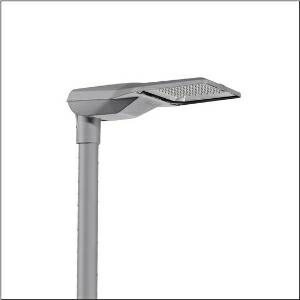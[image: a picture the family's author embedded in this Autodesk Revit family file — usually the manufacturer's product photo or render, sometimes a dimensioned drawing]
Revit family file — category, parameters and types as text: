
# Revit family: streetlight_sl_21_iq_midi___stw1_0a_5xe3e31g08nb_66c1
name_source: partatom
category: Lighting Fixtures
units: mm (PartAtom-declared; Revit-internal decimal feet)

## family parameters
Cut with Voids When Loaded = No
Host = Face
Light Source = No
Part Type = Normal
Room Calculation Point = No
Round Connector Dimension = Use Diameter
Shared = No

## types (1)
- --- (1 x LED, 23230 lm, 155.5 W, 3000K)
    Apparent Load = 155 VA
    CIE Flux Codes = 39 75 98 100 100
    Color Rendering = 70
    Color Temperature = 3000K
    Default Elevation = 1800 mm
    Description = Streetlight SL 21 iQ midi, mast luminaire, primary light control with lens, of PMMA, primary optical cover: cover, of toughened safety glass, transparent, light distribution: STW1.0a, light emission: direct distribution, primary light characteristic: asymmetric, installation type: post-top, side-entry, LED, High Power LED, rated luminous flux: 23.230lm, luminous efficacy: 149lm/W, light colour: 730, colour temperature: 3000K, control gear: iQ Street-Remote, control: Street-Remote, Auto-Match, Temp-Guard, Lumen-Switch, Night-Set, Smart-Wire, Light-Fading, Desk-Remote (wireless, voltage-free reading and setting of iQ features in the workshop via application-optimized NFC function/RFID function), optimised constant luminous flux control (CLO 2.0), pre-setting: linear dimming characteristic, mains connection: 230..240V, AC, 50/60Hz, start of lifetime: 156W, end of service life: 162W, reduction: 69W, luminaire housing, of diecast aluminium, powder-coated, Siteco® metallic grey (DB 702S), corrosivity category C5 mid according to DIN EN ISO 12944, please order mast flange separately, inclination adjustable: 0°, 5°, 10°, 15°, sealing non-destructively replaceable, multi-level sealing system, length: 644mm, width: 335mm, height: 110mm, mast flange for spigot size: 42mm (side-entry): 5XC10008XM4, 60/48mm (side-entry/post-top): 5XC10108XM2, 76/60mm (side-entry/post-top): 5XC10108XM1, mounting height: 4..8m, protection rating (complete): IP66, insulation class (complete): insulation class II (safety insulation), certification: CE, ENEC, ENEC+, VDE, impact resistance: IK10, permissible operating ambient temperature for outdoor applications: -40..+50°C, standard-compliant lighting for roads and squares, packaging unit: 1 piece

Light Distribution: STW1.0a
    Height = 111 mm
    Lamp = 1 x LED
    Lamp Light Flux = 23230 lm
    Lamp Power = 155.5 W
    Lamp count = 1
    Length = 644 mm
    Luminous efficacy = 149 lm/W
    Manufacturer = Siteco
    ModVariant = No
    Model = 5XE3E31G08NB
    Number of Poles = 1
    OnlyDefault = Yes
    Power Factor = 1
    Product Name = Streetlight SL 21 iQ midi | STW1.0a
    Product group = mast luminaire | pylon top
    ProductGroupID = 6100
    Protection Class = Protection class II
    Protection Degree = IP 66
    RLX_Detail_Level = 1
    RLX_Emergency_Light_Flux = 0 lm
    RLX_Emergency_Type = 0
    RLX_Emergency_Type_DB = No
    RlxData = <blob elided: 27285 chars, md5=1be792d1>
    Socket = socket
    Standby Power = 0 W
    System Light Flux = 23230 lm
    System Power = 155 W
    Type Comments = factory setting: luminous flux: 100 % | dim-lin: 254 | 823 mA
    Type Image = l_1004298.jpg
    URL = http://relux.com
    VarID = @adj_169884
    Voltage = 0 V
    Weight = 0.00 kg
    Width = 336 mm

## geometry (parser evidence)
native form markers: Blend x4, Sweep x11
no freeform markers — native parametric forms only
